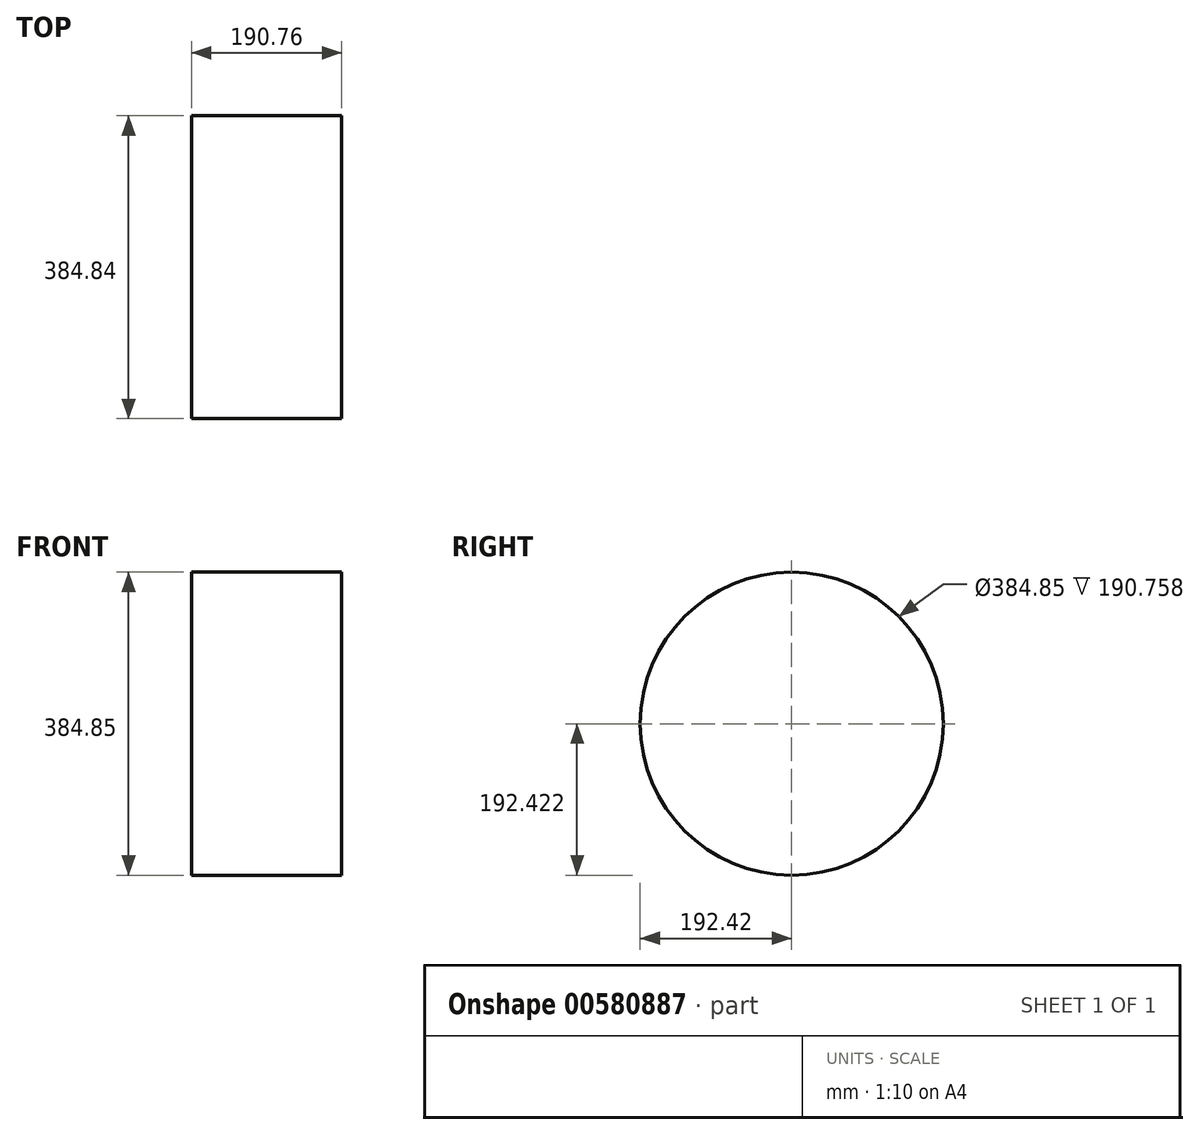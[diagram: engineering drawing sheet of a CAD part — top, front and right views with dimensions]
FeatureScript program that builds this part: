
annotation { "Feature Type Name" : "Feature", "Feature Type Description" : "" }
export const myFeature = defineFeature(function(context is Context, id is Id, definition is map)
    precondition{}
    {
        {
            var Q0;
            Q0=qCreatedBy(makeId("Front.planeOp"),FACE);
            var sketch = newSketch(context, id + "F0", { "sketchPlane" : qUnion([Q0])});
            skLineSegment(sketch, "E0.bottom", {"start": v(95.38, 96.21) * mm, "end": v(-95.38, 96.21) * mm, "construction": true});
            skLineSegment(sketch, "E0.top", {"start": v(95.38, -96.21) * mm, "end": v(-95.38, -96.21) * mm});
            skLineSegment(sketch, "E0.left", {"start": v(95.38, 96.21) * mm, "end": v(95.38, -96.21) * mm});
            skLineSegment(sketch, "E0.right", {"start": v(-95.38, 96.21) * mm, "end": v(-95.38, -96.21) * mm});
            skPoint(sketch, "E0.middle", {"position": v(0, 0) * mm});
            skSolve(sketch);
        }
        {
            var Q0;
            Q0 = qSketchRegion(id + "F0", true);
            var Q1;
            Q1=sQuery(id+"F0.wireOp",EDGE,"E0.top");
            var Q2;
            Q2=sQuery(id+"F0.wireOp",EDGE,"E0.left");
            var Q3;
            Q3=sQuery(id+"F0.wireOp",EDGE,"E0.right");
            var Q4;
            Q4=sQuery(id+"F0.wireOp",EDGE,"E0.bottom");
            revolve(context, id + "F1", {"bodyType" : ToolBodyType.SURFACE, "surfaceEntities" : qUnion([Q0, Q1, Q2, Q3]), "axis" : qUnion([Q4]), "revolveType" : RevolveType.FULL});
        }
    });
